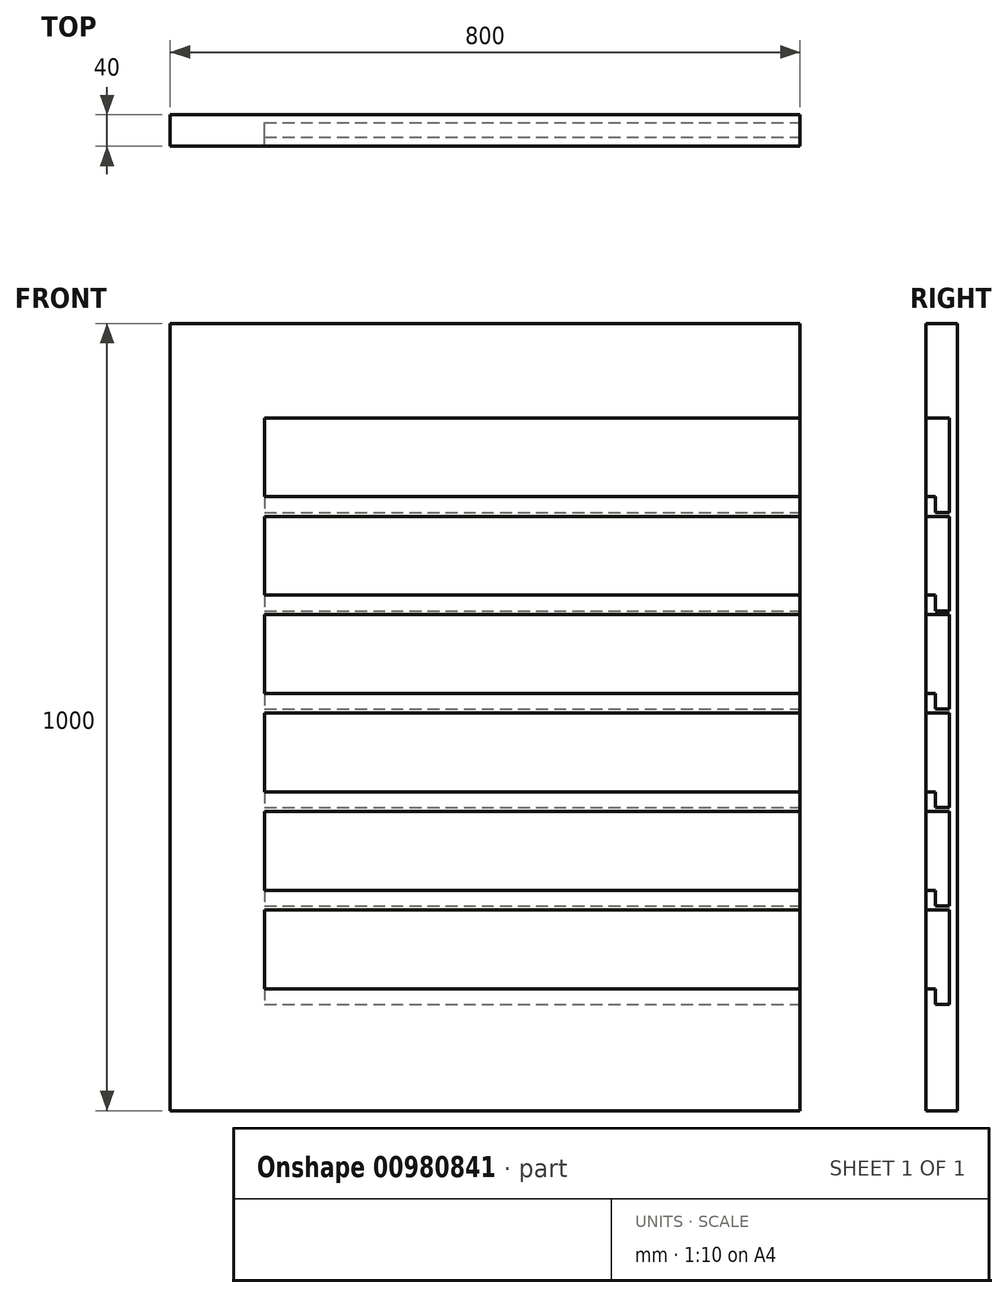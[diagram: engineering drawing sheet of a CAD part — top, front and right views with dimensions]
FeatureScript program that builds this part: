
annotation { "Feature Type Name" : "Feature", "Feature Type Description" : "" }
export const myFeature = defineFeature(function(context is Context, id is Id, definition is map)
    precondition{}
    {
        {
            var Q0;
            Q0=qCreatedBy(makeId("Front.planeOp"),FACE);
            var sketch = newSketch(context, id + "F0", { "sketchPlane" : qUnion([Q0])});
            skLineSegment(sketch, "E0.bottom", {"start": v(400, -500) * mm, "end": v(-400, -500) * mm});
            skLineSegment(sketch, "E0.top", {"start": v(400, 500) * mm, "end": v(-400, 500) * mm});
            skLineSegment(sketch, "E0.left", {"start": v(400, -500) * mm, "end": v(400, 500) * mm});
            skLineSegment(sketch, "E0.right", {"start": v(-400, -500) * mm, "end": v(-400, 500) * mm});
            skPoint(sketch, "E0.middle", {"position": v(0, 0) * mm});
            skSolve(sketch);
        }
        {
            var Q0;
            Q0=makeQuery(id+"F0.imprint","IMPRINT",FACE,{"disambiguationData":[TD([[makeQuery(id+"F0.imprint","IMPRINT",EDGE,{"derivedFrom":sQuery(id+"F0.wireOp",EDGE,"E0.bottom")}),-1.0]])]});
            extrude(context, id + "F1", {"entities" : qUnion([Q0]), "depth" : 10 * mm, "offsetDistance" : 25 * mm});
        }
        {
            var Q0;
            Q0=makeQuery(id+"F1.opExtrude","CAP_FACE",FACE,{"disambiguationData":[OSD([sQuery(id+"F0.wireOp",EDGE,"E0.bottom"),sQuery(id+"F0.wireOp",EDGE,"E0.top"),sQuery(id+"F0.wireOp",EDGE,"E0.left"),sQuery(id+"F0.wireOp",EDGE,"E0.right")])],"isStart":false});
            var sketch = newSketch(context, id + "F2", { "sketchPlane" : qUnion([Q0])});
            skLineSegment(sketch, "E1.bottom", {"start": v(-400, 500) * mm, "end": v(400, 500) * mm});
            skLineSegment(sketch, "E1.top", {"start": v(-400, 380) * mm, "end": v(400, 380) * mm});
            skLineSegment(sketch, "E1.left", {"start": v(-400, 500) * mm, "end": v(-400, 380) * mm});
            skLineSegment(sketch, "E1.right", {"start": v(400, 500) * mm, "end": v(400, 380) * mm});
            skLineSegment(sketch, "E2.bottom", {"start": v(-400, 500) * mm, "end": v(-280, 500) * mm});
            skLineSegment(sketch, "E2.top", {"start": v(-400, -500) * mm, "end": v(-280, -500) * mm});
            skLineSegment(sketch, "E2.left", {"start": v(-400, 500) * mm, "end": v(-400, -500) * mm});
            skLineSegment(sketch, "E2.right", {"start": v(-280, 500) * mm, "end": v(-280, -500) * mm});
            skSolve(sketch);
        }
        {
            var Q0;
            {var subQ0=sQuery(id+"F2.wireOp",EDGE,"E1.bottom");Q0=makeQuery(id+"F2.imprint","IMPRINT",FACE,{"disambiguationData":[TD([[makeQuery(id+"F2.imprint","IMPRINT",EDGE,{"derivedFrom":subQ0}),1.0]])]});}
            var Q1;
            {var subQ5=sQuery(id+"F2.wireOp",EDGE,"E2.top");Q1=makeQuery(id+"F2.imprint","IMPRINT",FACE,{"disambiguationData":[TD([[makeQuery(id+"F2.imprint","IMPRINT",EDGE,{"derivedFrom":subQ5}),-1.0]])]});}
            var Q2;
            {var subQ5=sQuery(id+"F2.wireOp",EDGE,"E2.bottom");Q2=makeQuery(id+"F2.imprint","IMPRINT",FACE,{"disambiguationData":[TD([[makeQuery(id+"F2.imprint","IMPRINT",EDGE,{"derivedFrom":subQ5}),1.0]])]});}
            extrude(context, id + "F3", {"entities" : qUnion([Q0, Q1, Q2]), "operationType" : NewBodyOperationType.ADD, "depth" : 30 * mm, "offsetDistance" : 25 * mm});
        }
        {
            var Q0;
            Q0=makeQuery(id+"F3.opExtrude","SWEPT_FACE",FACE,{"disambiguationData":[OSD([sQuery(id+"F2.wireOp",EDGE,"E2.right")])]});
            var sketch = newSketch(context, id + "F4", { "sketchPlane" : qUnion([Q0])});
            skLineSegment(sketch, "E3.bottom", {"start": v(-40, 280) * mm, "end": v(-10, 280) * mm});
            skLineSegment(sketch, "E3.top", {"start": v(-40, 255) * mm, "end": v(-10, 255) * mm});
            skLineSegment(sketch, "E3.left", {"start": v(-40, 280) * mm, "end": v(-40, 255) * mm});
            skLineSegment(sketch, "E3.right", {"start": v(-10, 280) * mm, "end": v(-10, 255) * mm});
            skLineSegment(sketch, "E4.bottom", {"start": v(-40, 155) * mm, "end": v(-10, 155) * mm});
            skLineSegment(sketch, "E4.top", {"start": v(-40, 130) * mm, "end": v(-10, 130) * mm});
            skLineSegment(sketch, "E4.left", {"start": v(-40, 155) * mm, "end": v(-40, 130) * mm});
            skLineSegment(sketch, "E4.right", {"start": v(-10, 155) * mm, "end": v(-10, 130) * mm});
            skLineSegment(sketch, "E5.bottom", {"start": v(-40, 30) * mm, "end": v(-10, 30) * mm});
            skLineSegment(sketch, "E5.top", {"start": v(-40, 5) * mm, "end": v(-10, 5) * mm});
            skLineSegment(sketch, "E5.left", {"start": v(-40, 30) * mm, "end": v(-40, 5) * mm});
            skLineSegment(sketch, "E5.right", {"start": v(-10, 30) * mm, "end": v(-10, 5) * mm});
            skLineSegment(sketch, "E6.bottom", {"start": v(-40, -95) * mm, "end": v(-10, -95) * mm});
            skLineSegment(sketch, "E6.top", {"start": v(-40, -120) * mm, "end": v(-10, -120) * mm});
            skLineSegment(sketch, "E6.left", {"start": v(-40, -95) * mm, "end": v(-40, -120) * mm});
            skLineSegment(sketch, "E6.right", {"start": v(-10, -95) * mm, "end": v(-10, -120) * mm});
            skLineSegment(sketch, "E7.bottom", {"start": v(-40, -220) * mm, "end": v(-10, -220) * mm});
            skLineSegment(sketch, "E7.top", {"start": v(-40, -245) * mm, "end": v(-10, -245) * mm});
            skLineSegment(sketch, "E7.left", {"start": v(-40, -220) * mm, "end": v(-40, -245) * mm});
            skLineSegment(sketch, "E7.right", {"start": v(-10, -220) * mm, "end": v(-10, -245) * mm});
            skLineSegment(sketch, "E8.bottom", {"start": v(-40, -345) * mm, "end": v(-10, -345) * mm});
            skLineSegment(sketch, "E8.top", {"start": v(-40, -370) * mm, "end": v(-10, -370) * mm});
            skLineSegment(sketch, "E8.left", {"start": v(-40, -345) * mm, "end": v(-40, -370) * mm});
            skLineSegment(sketch, "E8.right", {"start": v(-10, -345) * mm, "end": v(-10, -370) * mm});
            skSolve(sketch);
        }
        {
            var Q0;
            Q0=makeQuery(id+"F4.imprint","IMPRINT",FACE,{"disambiguationData":[TD([[makeQuery(id+"F4.imprint","IMPRINT",EDGE,{"derivedFrom":sQuery(id+"F4.wireOp",EDGE,"E3.bottom")}),-1.0]])]});
            var Q1;
            Q1=makeQuery(id+"F4.imprint","IMPRINT",FACE,{"disambiguationData":[TD([[makeQuery(id+"F4.imprint","IMPRINT",EDGE,{"derivedFrom":sQuery(id+"F4.wireOp",EDGE,"E4.bottom")}),-1.0]])]});
            var Q2;
            Q2=makeQuery(id+"F4.imprint","IMPRINT",FACE,{"disambiguationData":[TD([[makeQuery(id+"F4.imprint","IMPRINT",EDGE,{"derivedFrom":sQuery(id+"F4.wireOp",EDGE,"E5.bottom")}),-1.0]])]});
            var Q3;
            Q3=makeQuery(id+"F4.imprint","IMPRINT",FACE,{"disambiguationData":[TD([[makeQuery(id+"F4.imprint","IMPRINT",EDGE,{"derivedFrom":sQuery(id+"F4.wireOp",EDGE,"E6.bottom")}),-1.0]])]});
            var Q4;
            Q4=makeQuery(id+"F4.imprint","IMPRINT",FACE,{"disambiguationData":[TD([[makeQuery(id+"F4.imprint","IMPRINT",EDGE,{"derivedFrom":sQuery(id+"F4.wireOp",EDGE,"E7.bottom")}),-1.0]])]});
            var Q5;
            Q5=makeQuery(id+"F4.imprint","IMPRINT",FACE,{"disambiguationData":[TD([[makeQuery(id+"F4.imprint","IMPRINT",EDGE,{"derivedFrom":sQuery(id+"F4.wireOp",EDGE,"E8.bottom")}),-1.0]])]});
            var Q6;
            {var subQ0=sQuery(id+"F4.wireOp",EDGE,"E8.top");Q6=makeQuery(id+"F4.imprint","IMPRINT",FACE,{"disambiguationData":[TD([[makeQuery(id+"F4.imprint","IMPRINT",EDGE,{"derivedFrom":subQ0}),-1.0]])]});}
            extrude(context, id + "F5", {"entities" : qUnion([Q0, Q1, Q2, Q3, Q4, Q5, Q6]), "operationType" : NewBodyOperationType.ADD, "depth" : 680 * mm, "offsetDistance" : 25 * mm});
        }
        {
            var Q0;
            Q0=makeQuery(id+"F5.boolean.opBoolean","MERGE",FACE,{"derivedFrom":[makeQuery(id+"F3.boolean.opBoolean","MERGE",FACE,{"derivedFrom":[makeQuery(id+"F1.opExtrude","SWEPT_FACE",FACE,{"disambiguationData":[OSD([sQuery(id+"F0.wireOp",EDGE,"E0.left")])]}),makeQuery(id+"F3.opExtrude","SWEPT_FACE",FACE,{"disambiguationData":[OSD([sQuery(id+"F2.wireOp",EDGE,"E1.right")])]})]}),makeQuery(id+"F5.opExtrude","CAP_FACE",FACE,{"disambiguationData":[OSD([sQuery(id+"F4.wireOp",EDGE,"E3.bottom"),sQuery(id+"F4.wireOp",EDGE,"E3.top"),sQuery(id+"F4.wireOp",EDGE,"E3.left"),sQuery(id+"F4.wireOp",EDGE,"E3.right")])],"isStart":false}),makeQuery(id+"F5.opExtrude","CAP_FACE",FACE,{"disambiguationData":[OSD([sQuery(id+"F4.wireOp",EDGE,"E4.bottom"),sQuery(id+"F4.wireOp",EDGE,"E4.top"),sQuery(id+"F4.wireOp",EDGE,"E4.left"),sQuery(id+"F4.wireOp",EDGE,"E4.right")])],"isStart":false}),makeQuery(id+"F5.opExtrude","CAP_FACE",FACE,{"disambiguationData":[OSD([sQuery(id+"F4.wireOp",EDGE,"E5.bottom"),sQuery(id+"F4.wireOp",EDGE,"E5.top"),sQuery(id+"F4.wireOp",EDGE,"E5.left"),sQuery(id+"F4.wireOp",EDGE,"E5.right")])],"isStart":false}),makeQuery(id+"F5.opExtrude","CAP_FACE",FACE,{"disambiguationData":[OSD([sQuery(id+"F4.wireOp",EDGE,"E6.bottom"),sQuery(id+"F4.wireOp",EDGE,"E6.top"),sQuery(id+"F4.wireOp",EDGE,"E6.left"),sQuery(id+"F4.wireOp",EDGE,"E6.right")])],"isStart":false}),makeQuery(id+"F5.opExtrude","CAP_FACE",FACE,{"disambiguationData":[OSD([sQuery(id+"F4.wireOp",EDGE,"E7.bottom"),sQuery(id+"F4.wireOp",EDGE,"E7.top"),sQuery(id+"F4.wireOp",EDGE,"E7.left"),sQuery(id+"F4.wireOp",EDGE,"E7.right")])],"isStart":false}),makeQuery(id+"F5.opExtrude","CAP_FACE",FACE,{"disambiguationData":[OSD([sQuery(id+"F0.wireOp",EDGE,"E0.bottom"),sQuery(id+"F2.wireOp",EDGE,"E2.top"),sQuery(id+"F2.wireOp",EDGE,"E2.right"),sQuery(id+"F4.wireOp",EDGE,"E8.bottom"),sQuery(id+"F4.wireOp",EDGE,"E8.left"),sQuery(id+"F4.wireOp",EDGE,"E8.right")])],"isStart":false})]});
            var sketch = newSketch(context, id + "F6", { "sketchPlane" : qUnion([Q0])});
            skLineSegment(sketch, "E9.bottom", {"start": v(-28, 280) * mm, "end": v(-10, 280) * mm});
            skLineSegment(sketch, "E9.top", {"start": v(-28, 260) * mm, "end": v(-10, 260) * mm});
            skLineSegment(sketch, "E9.left", {"start": v(-28, 280) * mm, "end": v(-28, 260) * mm});
            skLineSegment(sketch, "E9.right", {"start": v(-10, 280) * mm, "end": v(-10, 260) * mm});
            skLineSegment(sketch, "E10.bottom", {"start": v(-28, 155) * mm, "end": v(-10, 155) * mm});
            skLineSegment(sketch, "E10.top", {"start": v(-28, 135) * mm, "end": v(-10, 135) * mm});
            skLineSegment(sketch, "E10.left", {"start": v(-28, 155) * mm, "end": v(-28, 135) * mm});
            skLineSegment(sketch, "E10.right", {"start": v(-10, 155) * mm, "end": v(-10, 135) * mm});
            skLineSegment(sketch, "E11.bottom", {"start": v(-28, 30) * mm, "end": v(-10, 30) * mm});
            skLineSegment(sketch, "E11.top", {"start": v(-28, 10) * mm, "end": v(-10, 10) * mm});
            skLineSegment(sketch, "E11.left", {"start": v(-28, 30) * mm, "end": v(-28, 10) * mm});
            skLineSegment(sketch, "E11.right", {"start": v(-10, 30) * mm, "end": v(-10, 10) * mm});
            skLineSegment(sketch, "E12.bottom", {"start": v(-28, -95) * mm, "end": v(-10, -95) * mm});
            skLineSegment(sketch, "E12.top", {"start": v(-28, -115) * mm, "end": v(-10, -115) * mm});
            skLineSegment(sketch, "E12.left", {"start": v(-28, -95) * mm, "end": v(-28, -115) * mm});
            skLineSegment(sketch, "E12.right", {"start": v(-10, -95) * mm, "end": v(-10, -115) * mm});
            skLineSegment(sketch, "E13.bottom", {"start": v(-28, -220) * mm, "end": v(-10, -220) * mm});
            skLineSegment(sketch, "E13.top", {"start": v(-28, -240) * mm, "end": v(-10, -240) * mm});
            skLineSegment(sketch, "E13.left", {"start": v(-28, -220) * mm, "end": v(-28, -240) * mm});
            skLineSegment(sketch, "E13.right", {"start": v(-10, -220) * mm, "end": v(-10, -240) * mm});
            skLineSegment(sketch, "E14.bottom", {"start": v(-28, -345) * mm, "end": v(-10, -345) * mm});
            skLineSegment(sketch, "E14.top", {"start": v(-28, -365) * mm, "end": v(-10, -365) * mm});
            skLineSegment(sketch, "E14.left", {"start": v(-28, -345) * mm, "end": v(-28, -365) * mm});
            skLineSegment(sketch, "E14.right", {"start": v(-10, -345) * mm, "end": v(-10, -365) * mm});
            skSolve(sketch);
        }
        {
            var Q0;
            Q0=makeQuery(id+"F6.imprint","IMPRINT",FACE,{"disambiguationData":[TD([[makeQuery(id+"F6.imprint","IMPRINT",EDGE,{"derivedFrom":sQuery(id+"F6.wireOp",EDGE,"E9.bottom")}),-1.0]])]});
            var Q1;
            Q1=makeQuery(id+"F6.imprint","IMPRINT",FACE,{"disambiguationData":[TD([[makeQuery(id+"F6.imprint","IMPRINT",EDGE,{"derivedFrom":sQuery(id+"F6.wireOp",EDGE,"E10.bottom")}),-1.0]])]});
            var Q2;
            Q2=makeQuery(id+"F6.imprint","IMPRINT",FACE,{"disambiguationData":[TD([[makeQuery(id+"F6.imprint","IMPRINT",EDGE,{"derivedFrom":sQuery(id+"F6.wireOp",EDGE,"E11.bottom")}),-1.0]])]});
            var Q3;
            Q3=makeQuery(id+"F6.imprint","IMPRINT",FACE,{"disambiguationData":[TD([[makeQuery(id+"F6.imprint","IMPRINT",EDGE,{"derivedFrom":sQuery(id+"F6.wireOp",EDGE,"E12.bottom")}),-1.0]])]});
            var Q4;
            Q4=makeQuery(id+"F6.imprint","IMPRINT",FACE,{"disambiguationData":[TD([[makeQuery(id+"F6.imprint","IMPRINT",EDGE,{"derivedFrom":sQuery(id+"F6.wireOp",EDGE,"E13.bottom")}),-1.0]])]});
            var Q5;
            Q5=makeQuery(id+"F6.imprint","IMPRINT",FACE,{"disambiguationData":[TD([[makeQuery(id+"F6.imprint","IMPRINT",EDGE,{"derivedFrom":sQuery(id+"F6.wireOp",EDGE,"E14.bottom")}),-1.0]])]});
            extrude(context, id + "F7", {"entities" : qUnion([Q0, Q1, Q2, Q3, Q4, Q5]), "operationType" : NewBodyOperationType.REMOVE, "oppositeDirection" : true, "depth" : 680 * mm, "offsetDistance" : 25 * mm});
        }
    });
